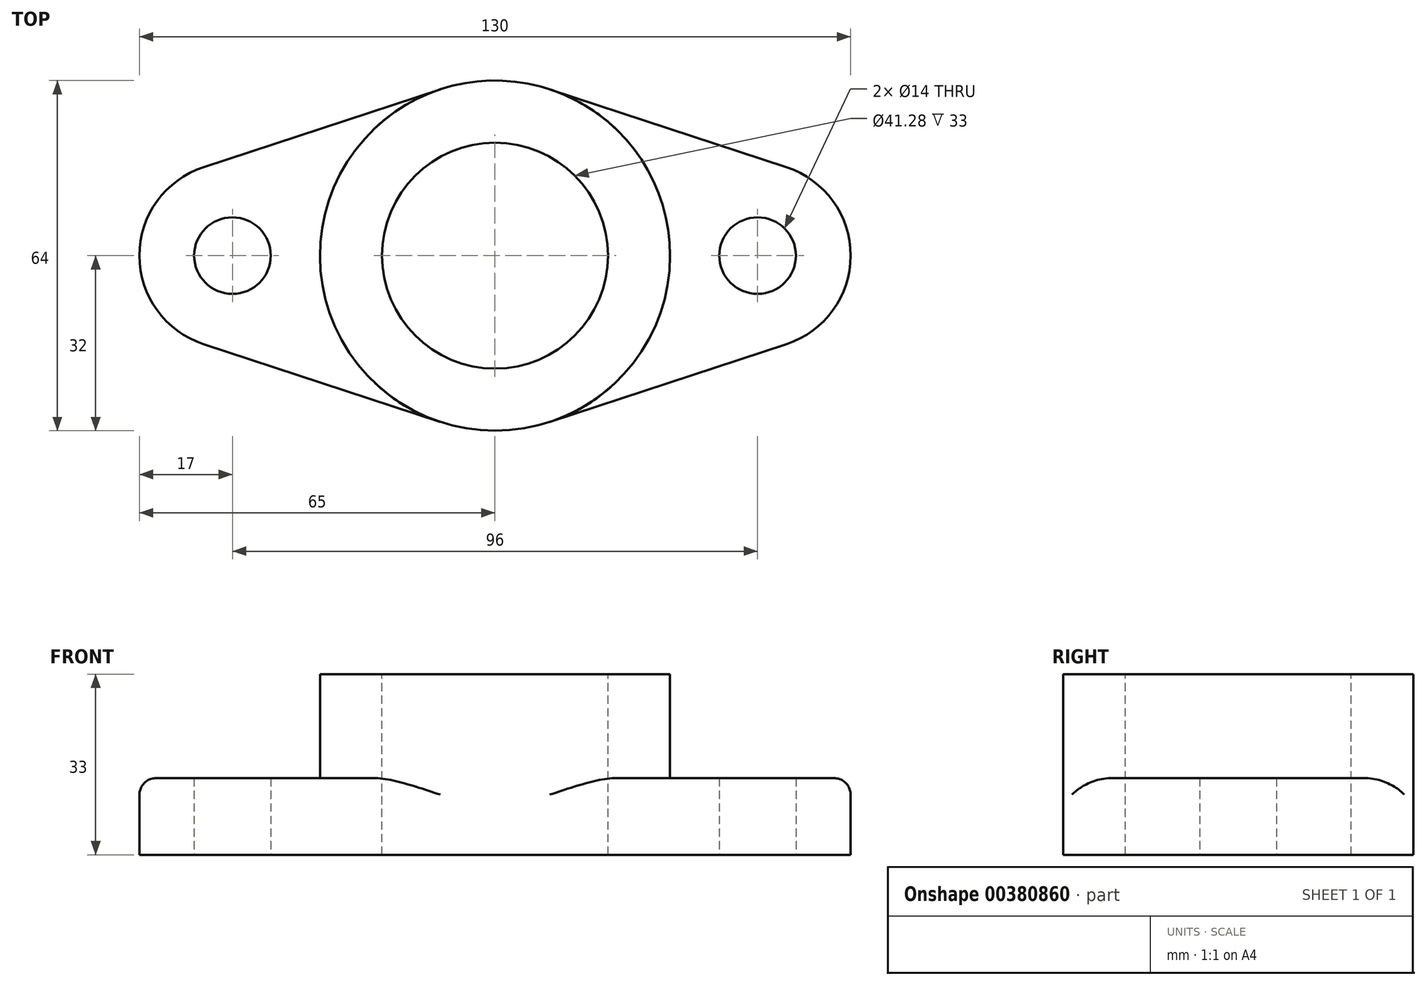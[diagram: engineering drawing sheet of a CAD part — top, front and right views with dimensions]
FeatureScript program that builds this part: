
annotation { "Feature Type Name" : "Feature", "Feature Type Description" : "" }
export const myFeature = defineFeature(function(context is Context, id is Id, definition is map)
    precondition{}
    {
        {
            var Q0;
            Q0=qCreatedBy(makeId("Top.planeOp"),FACE);
            var sketch = newSketch(context, id + "F0", { "sketchPlane" : qUnion([Q0])});
            skCircle(sketch, "E0", {"center": v(0, 0) * mm, "radius": 32 * mm});
            skLineSegment(sketch, "E1", {"start": v(-53.31, 16.15) * mm, "end": v(-10, 30.4) * mm});
            skLineSegment(sketch, "E2", {"start": v(-53.31, -16.15) * mm, "end": v(-10, -30.4) * mm});
            skLineSegment(sketch, "E3", {"start": v(10, 30.4) * mm, "end": v(53.31, 16.15) * mm});
            skLineSegment(sketch, "E4", {"start": v(10, -30.4) * mm, "end": v(53.31, -16.15) * mm});
            skCircle(sketch, "E5", {"center": v(-48, 0) * mm, "radius": 7 * mm});
            skCircle(sketch, "E6", {"center": v(48, 0) * mm, "radius": 7 * mm});
            skArc(sketch, "E7", {"start": v(-53.31, 16.15) * mm, "mid": v(-65, 0) * mm, "end": v(-53.31, -16.15) * mm});
            skArc(sketch, "E8", {"start": v(53.31, -16.15) * mm, "mid": v(65, 0) * mm, "end": v(53.31, 16.15) * mm});
            skPoint(sketch, "E9.orphan", {"position": v(-39.37, 14.65) * mm});
            skPoint(sketch, "E10.orphan", {"position": v(-39.37, -14.65) * mm});
            skPoint(sketch, "E11.orphan", {"position": v(40.24, -15.13) * mm});
            skPoint(sketch, "E12.orphan", {"position": v(40.24, 15.13) * mm});
            skSolve(sketch);
        }
        {
            var Q0;
            {var subQ0=sQuery(id+"F0.wireOp",EDGE,"E0");var subQ1=makeQuery(id+"F0.imprint","INTERSECT",VERTEX,{"derivedFrom":[subQ0,sQuery(id+"F0.wireOp",EDGE,"E1")]});Q0=makeQuery(id+"F0.imprint","IMPRINT",FACE,{"disambiguationData":[TD([[makeQuery(id+"F0.imprint","IMPRINT",EDGE,{"disambiguationData":[TD([[subQ1,1.0]])],"derivedFrom":subQ0}),1.0]])]});}
            extrude(context, id + "F1", {"entities" : qUnion([Q0]), "depth" : 33 * mm});
        }
        {
            var Q0;
            {var subQ0=sQuery(id+"F0.wireOp",EDGE,"E1");Q0=makeQuery(id+"F0.imprint","IMPRINT",FACE,{"disambiguationData":[TD([[makeQuery(id+"F0.imprint","IMPRINT",EDGE,{"derivedFrom":subQ0}),-1.0]])]});}
            var Q1;
            {var subQ0=sQuery(id+"F0.wireOp",EDGE,"fzxDVFEc-3jti-53vk-N4eU-vg0HHvl4Yq9Q");var subQ1=makeQuery(id+"F0.imprint","INTERSECT",VERTEX,{"derivedFrom":[subQ0,sQuery(id+"F0.wireOp",EDGE,"E1")]});Q1=makeQuery(id+"F0.imprint","IMPRINT",FACE,{"disambiguationData":[TD([[makeQuery(id+"F0.imprint","IMPRINT",EDGE,{"disambiguationData":[TD([[subQ1,-1.0]])],"derivedFrom":subQ0}),1.0]])]});}
            var Q2;
            {var subQ0=sQuery(id+"F0.wireOp",EDGE,"E3");Q2=makeQuery(id+"F0.imprint","IMPRINT",FACE,{"disambiguationData":[TD([[makeQuery(id+"F0.imprint","IMPRINT",EDGE,{"derivedFrom":subQ0}),-1.0]])]});}
            var Q3;
            {var subQ0=sQuery(id+"F0.wireOp",EDGE,"INIp07KA-PeCi-i1cB-SN0W-P3niCgjrsPL2");var subQ1=makeQuery(id+"F0.imprint","INTERSECT",VERTEX,{"derivedFrom":[subQ0,sQuery(id+"F0.wireOp",EDGE,"E3")]});Q3=makeQuery(id+"F0.imprint","IMPRINT",FACE,{"disambiguationData":[TD([[makeQuery(id+"F0.imprint","IMPRINT",EDGE,{"disambiguationData":[TD([[subQ1,-1.0]])],"derivedFrom":subQ0}),1.0]])]});}
            extrude(context, id + "F2", {"entities" : qUnion([Q0, Q1, Q2, Q3]), "operationType" : NewBodyOperationType.ADD, "depth" : 14 * mm});
        }
        {
            var Q0;
            Q0=makeQuery(id+"F1.opExtrude","CAP_FACE",FACE,{"disambiguationData":[OSD([sQuery(id+"F0.wireOp",EDGE,"E0")])],"isStart":false});
            var sketch = newSketch(context, id + "F3", { "sketchPlane" : qUnion([Q0])});
            skCircle(sketch, "E13", {"center": v(0, 0) * mm, "radius": 20.64 * mm});
            skSolve(sketch);
        }
        {
            var Q0;
            Q0=makeQuery(id+"F3.imprint","IMPRINT",FACE,{"disambiguationData":[TD([[makeQuery(id+"F3.imprint","IMPRINT",EDGE,{"derivedFrom":sQuery(id+"F3.wireOp",EDGE,"E13")}),1.0]])]});
            extrude(context, id + "F4", {"entities" : qUnion([Q0]), "operationType" : NewBodyOperationType.REMOVE, "endBound" : BoundingType.THROUGH_ALL, "oppositeDirection" : true, "depth" : 25 * mm});
        }
        {
            var Q0;
            Q0=makeQuery(id+"F2.opExtrude","CAP_EDGE",EDGE,{"disambiguationData":[OSD([sQuery(id+"F0.wireOp",EDGE,"E7")])],"isStart":false});
            var Q1;
            Q1=makeQuery(id+"F2.opExtrude","CAP_EDGE",EDGE,{"disambiguationData":[OSD([sQuery(id+"F0.wireOp",EDGE,"E8")])],"isStart":false});
            var Q2;
            {var subQ0=sQuery(id+"F0.wireOp",EDGE,"E0");Q2=makeQuery(id+"F2.opExtrude","CAP_EDGE",EDGE,{"disambiguationData":[OSD([subQ0]),TDD([makeQuery(id+"F0.imprint","IMPRINT",EDGE,{"disambiguationData":[TD([[makeQuery(id+"F0.imprint","INTERSECT",VERTEX,{"derivedFrom":[subQ0,sQuery(id+"F0.wireOp",EDGE,"E1")]}),-1.0]])],"derivedFrom":subQ0})])],"isStart":false});}
            var Q3;
            {var subQ0=sQuery(id+"F0.wireOp",EDGE,"E0");Q3=makeQuery(id+"F2.opExtrude","CAP_EDGE",EDGE,{"disambiguationData":[OSD([subQ0]),TDD([makeQuery(id+"F0.imprint","IMPRINT",EDGE,{"disambiguationData":[TD([[makeQuery(id+"F0.imprint","INTERSECT",VERTEX,{"derivedFrom":[subQ0,sQuery(id+"F0.wireOp",EDGE,"E3")]}),1.0]])],"derivedFrom":subQ0})])],"isStart":false});}
            fillet(context, id + "F5", {"entities" : qUnion([Q0, Q1, Q2, Q3]), "radius" : 3 * mm, "tangentPropagation" : true, "allowEdgeOverflow" : false});
        }
    });
